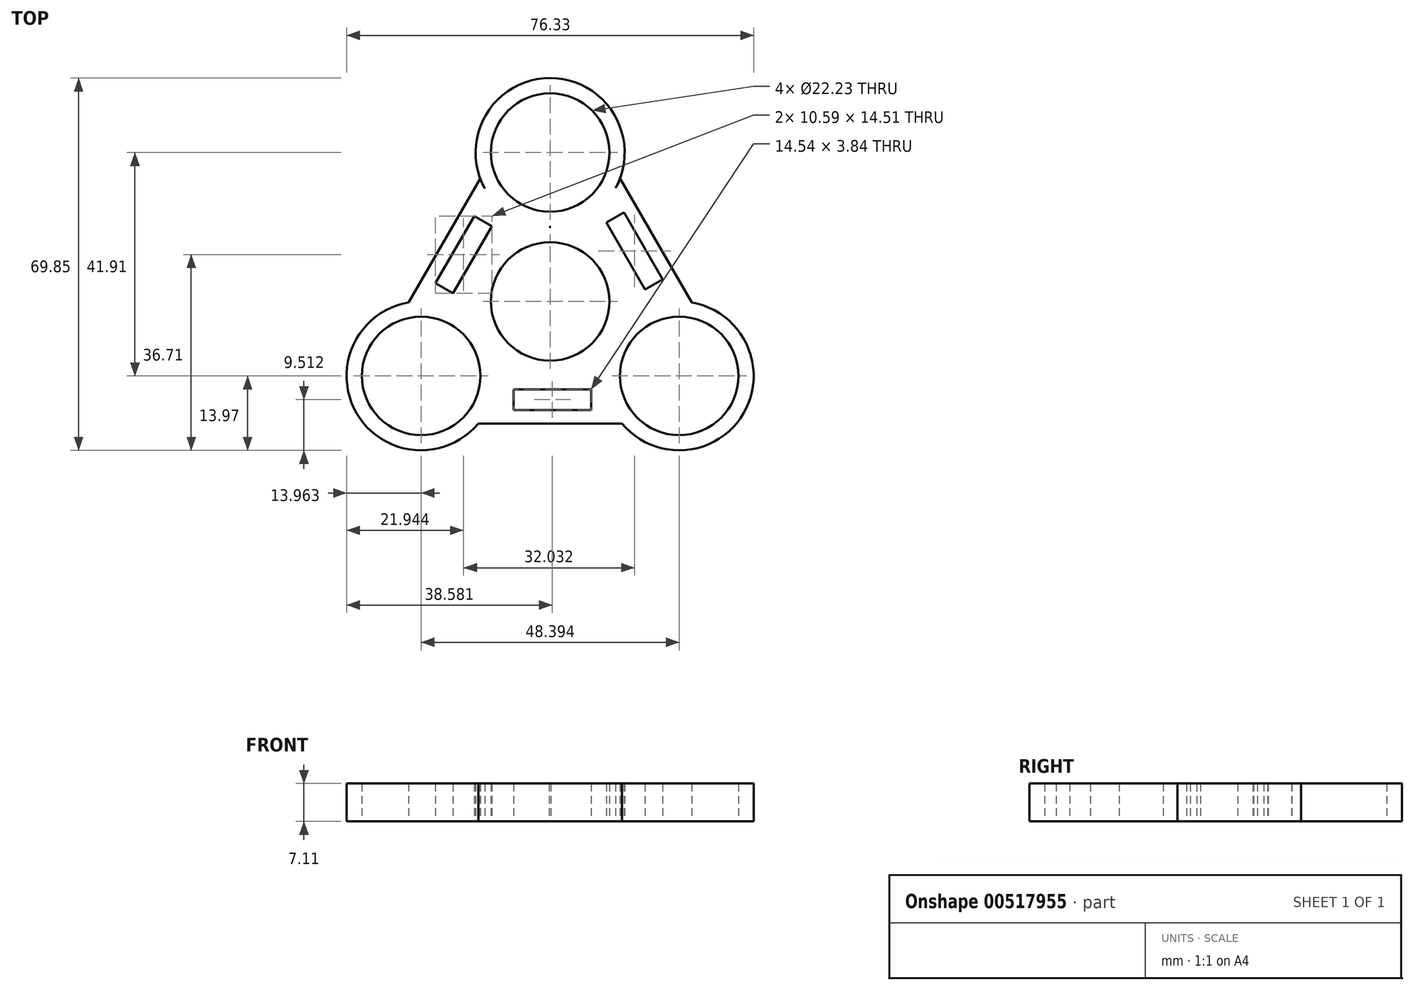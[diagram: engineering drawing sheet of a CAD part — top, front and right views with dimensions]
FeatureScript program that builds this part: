
annotation { "Feature Type Name" : "Feature", "Feature Type Description" : "" }
export const myFeature = defineFeature(function(context is Context, id is Id, definition is map)
    precondition{}
    {
        {
            var Q0;
            Q0=qCreatedBy(makeId("Top.planeOp"),FACE);
            var sketch = newSketch(context, id + "F0", { "sketchPlane" : qUnion([Q0])});
            skCircle(sketch, "E0", {"center": v(0, 0) * mm, "radius": 13.97 * mm});
            skCircle(sketch, "E1", {"center": v(0, 0) * mm, "radius": 11.11 * mm});
            skCircle(sketch, "E2", {"center": v(24.2, -13.97) * mm, "radius": 13.97 * mm});
            skCircle(sketch, "E3", {"center": v(24.2, -13.97) * mm, "radius": 11.11 * mm});
            skCircle(sketch, "E4", {"center": v(-24.2, -13.97) * mm, "radius": 13.97 * mm});
            skCircle(sketch, "E5", {"center": v(-24.2, -13.97) * mm, "radius": 11.11 * mm});
            skCircle(sketch, "E6", {"center": v(0, 27.94) * mm, "radius": 13.97 * mm});
            skCircle(sketch, "E7", {"center": v(0, 27.94) * mm, "radius": 11.11 * mm});
            skLineSegment(sketch, "E8", {"start": v(-6.99, 15.84) * mm, "end": v(6.99, 15.84) * mm});
            skLineSegment(sketch, "E9", {"start": v(6.99, 15.84) * mm, "end": v(17.21, -1.87) * mm});
            skLineSegment(sketch, "E10", {"start": v(17.21, -1.87) * mm, "end": v(10.23, -13.97) * mm});
            skLineSegment(sketch, "E11", {"start": v(10.23, -13.97) * mm, "end": v(-10.23, -13.97) * mm});
            skLineSegment(sketch, "E12", {"start": v(-10.23, -13.97) * mm, "end": v(-17.21, -1.87) * mm});
            skLineSegment(sketch, "E13", {"start": v(-6.99, 15.84) * mm, "end": v(-17.21, -1.87) * mm});
            skLineSegment(sketch, "E14", {"start": v(-13.45, -22.89) * mm, "end": v(13.44, -22.89) * mm});
            skLineSegment(sketch, "E15.bottom", {"start": v(-6.85, -16.5) * mm, "end": v(7.7, -16.5) * mm});
            skLineSegment(sketch, "E15.top", {"start": v(-6.85, -20.35) * mm, "end": v(7.7, -20.35) * mm});
            skLineSegment(sketch, "E15.left", {"start": v(-6.85, -16.5) * mm, "end": v(-6.85, -20.35) * mm});
            skLineSegment(sketch, "E15.right", {"start": v(7.7, -16.5) * mm, "end": v(7.7, -20.35) * mm});
            skLineSegment(sketch, "E16", {"start": v(26.61, -0.32) * mm, "end": v(13.17, 22.97) * mm});
            skLineSegment(sketch, "E17.bottom", {"start": v(17.79, 2.2) * mm, "end": v(10.52, 14.8) * mm});
            skLineSegment(sketch, "E17.top", {"start": v(21.11, 4.13) * mm, "end": v(13.84, 16.72) * mm});
            skLineSegment(sketch, "E17.left", {"start": v(17.79, 2.2) * mm, "end": v(21.11, 4.13) * mm});
            skLineSegment(sketch, "E17.right", {"start": v(10.52, 14.8) * mm, "end": v(13.84, 16.72) * mm});
            skLineSegment(sketch, "E18", {"start": v(-13.14, 23) * mm, "end": v(-26.59, -0.28) * mm});
            skLineSegment(sketch, "E19.bottom", {"start": v(-10.92, 14.1) * mm, "end": v(-18.19, 1.51) * mm});
            skLineSegment(sketch, "E19.top", {"start": v(-14.24, 16.02) * mm, "end": v(-21.51, 3.43) * mm});
            skLineSegment(sketch, "E19.left", {"start": v(-10.92, 14.1) * mm, "end": v(-14.24, 16.02) * mm});
            skLineSegment(sketch, "E19.right", {"start": v(-18.19, 1.51) * mm, "end": v(-21.51, 3.43) * mm});
            skArc(sketch, "E20", {"start": v(-13.14, 23) * mm, "mid": v(-10.63, 18.94) * mm, "end": v(-6.99, 15.84) * mm});
            skArc(sketch, "E21", {"start": v(6.99, 15.84) * mm, "mid": v(10.6, 18.95) * mm, "end": v(13.17, 22.97) * mm});
            skSolve(sketch);
        }
        {
            var Q0;
            Q0 = qSketchRegion(id + "F0", true);
            var Q1;
            {var subQ0=sQuery(id+"F0.wireOp",EDGE,"E6");var subQ1=sQuery(id+"F0.wireOp",EDGE,"E0");var subQ2=makeQuery(id+"F0.imprint","INTERSECT",VERTEX,{"disambiguationData":[OD(1.0)],"derivedFrom":[subQ1,subQ0]});Q1=makeQuery(id+"F0.imprint","IMPRINT",FACE,{"disambiguationData":[TD([[makeQuery(id+"F0.imprint","IMPRINT",EDGE,{"disambiguationData":[TD([[subQ2,-1.0]])],"derivedFrom":subQ1}),-1.0]])]});}
            var Q2;
            {var subQ4=sQuery(id+"F0.wireOp",EDGE,"E8");Q2=makeQuery(id+"F0.imprint","IMPRINT",FACE,{"disambiguationData":[TD([[makeQuery(id+"F0.imprint","IMPRINT",EDGE,{"derivedFrom":subQ4}),-1.0]])]});}
            var Q3;
            {var subQ0=sQuery(id+"F0.wireOp",EDGE,"E6");var subQ1=sQuery(id+"F0.wireOp",EDGE,"E0");var subQ2=makeQuery(id+"F0.imprint","INTERSECT",VERTEX,{"disambiguationData":[OD(0.0)],"derivedFrom":[subQ1,subQ0]});Q3=makeQuery(id+"F0.imprint","IMPRINT",FACE,{"disambiguationData":[TD([[makeQuery(id+"F0.imprint","IMPRINT",EDGE,{"disambiguationData":[TD([[subQ2,1.0]])],"derivedFrom":subQ1}),-1.0]])]});}
            var Q4;
            Q4=makeQuery(id+"F0.imprint","IMPRINT",FACE,{"disambiguationData":[TD([[makeQuery(id+"F0.imprint","IMPRINT",EDGE,{"derivedFrom":sQuery(id+"F0.wireOp",EDGE,"E1")}),-1.0]])]});
            var Q5;
            {var subQ0=sQuery(id+"F0.wireOp",EDGE,"E10");var subQ1=sQuery(id+"F0.wireOp",EDGE,"E2");var subQ3=makeQuery(id+"F0.imprint","INTERSECT",VERTEX,{"derivedFrom":[subQ1,subQ0]});Q5=makeQuery(id+"F0.imprint","IMPRINT",FACE,{"disambiguationData":[TD([[makeQuery(id+"F0.imprint","IMPRINT",EDGE,{"disambiguationData":[TD([[subQ3,1.0]])],"derivedFrom":subQ1}),1.0]])]});}
            var Q6;
            {var subQ0=sQuery(id+"F0.wireOp",EDGE,"E12");Q6=makeQuery(id+"F0.imprint","IMPRINT",FACE,{"disambiguationData":[TD([[makeQuery(id+"F0.imprint","IMPRINT",EDGE,{"derivedFrom":subQ0}),-1.0]])]});}
            var Q7;
            {var subQ0=sQuery(id+"F0.wireOp",EDGE,"E13");var subQ1=sQuery(id+"F0.wireOp",EDGE,"E0");var subQ2=makeQuery(id+"F0.imprint","INTERSECT",VERTEX,{"derivedFrom":[subQ1,subQ0]});Q7=makeQuery(id+"F0.imprint","IMPRINT",FACE,{"disambiguationData":[TD([[makeQuery(id+"F0.imprint","IMPRINT",EDGE,{"disambiguationData":[TD([[subQ2,-1.0]])],"derivedFrom":subQ1}),-1.0]])]});}
            var Q8;
            {var subQ1=sQuery(id+"F0.wireOp",EDGE,"E9");var subQ4=sQuery(id+"F0.wireOp",EDGE,"E0");var subQ5=makeQuery(id+"F0.imprint","INTERSECT",VERTEX,{"derivedFrom":[subQ4,subQ1]});Q8=makeQuery(id+"F0.imprint","IMPRINT",FACE,{"disambiguationData":[TD([[makeQuery(id+"F0.imprint","IMPRINT",EDGE,{"disambiguationData":[TD([[subQ5,1.0]])],"derivedFrom":subQ4}),-1.0]])]});}
            extrude(context, id + "F1", {"entities" : qUnion([Q0, Q1, Q2, Q3, Q4, Q5, Q6, Q7, Q8]), "depth" : 7.11 * mm, "offsetDistance" : 25.4 * mm});
        }
    });
